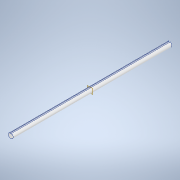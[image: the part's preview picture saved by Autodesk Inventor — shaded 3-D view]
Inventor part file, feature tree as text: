
AUTODESK INVENTOR PART (.ipt)
format: ipt  version: 2021 (Build 250183000, 183)  size: 102,400 bytes
history: native  units: in
note: dims shown in document units (in); Inventor stores cm internally (conversion verified against a paired STEP export)
features: extrude x1, sketch x1
ambient origin geometry x8: Origin, YZ Plane, XZ Plane, XY Plane, X Axis, Y Axis, Z Axis, Center Point
bodies: Solid1 (feature_tree)
feature tree (2):
  extrude  "Extrusion1"  [1 undecoded]
  sketch  "Sketch1"  dims[d4=0.0in]
note: 1 required parameter value undecoded (feature->parameter linkage not recoverable at this tier; creation-order binding heuristic only, values carry confidence <= 0.55)
